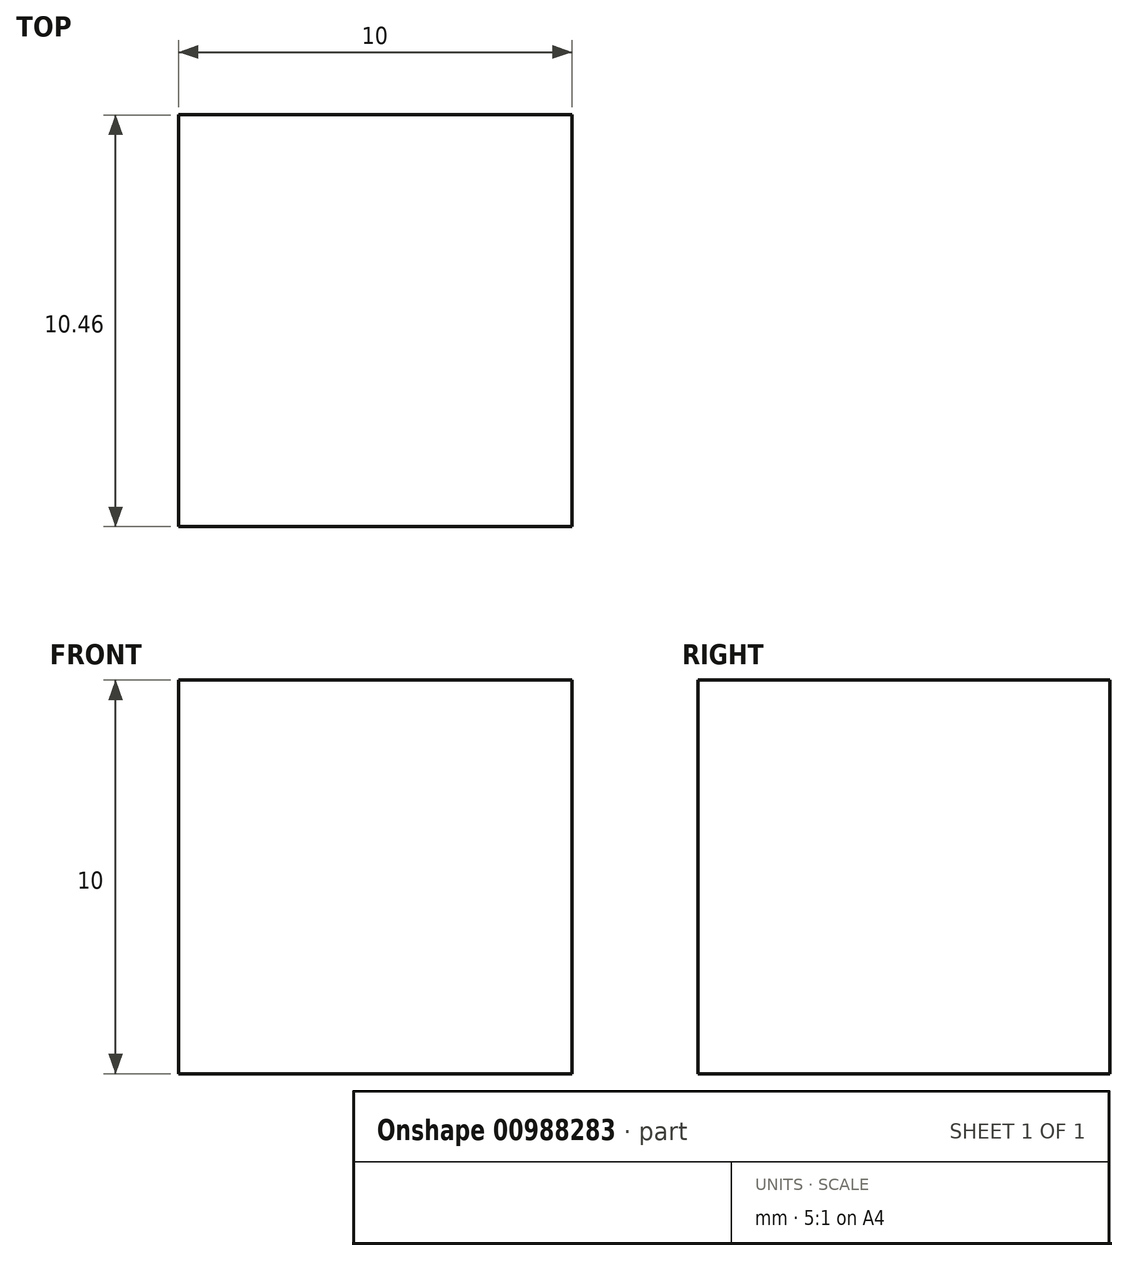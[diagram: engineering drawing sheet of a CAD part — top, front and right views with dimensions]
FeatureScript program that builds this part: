
annotation { "Feature Type Name" : "Feature", "Feature Type Description" : "" }
export const myFeature = defineFeature(function(context is Context, id is Id, definition is map)
    precondition{}
    {
        {
            var Q0;
            Q0=qCreatedBy(makeId("Top.planeOp"),FACE);
            var sketch = newSketch(context, id + "F0", { "sketchPlane" : qUnion([Q0])});
            skLineSegment(sketch, "E0.bottom", {"start": v(5, -5.23) * mm, "end": v(-5, -5.23) * mm});
            skLineSegment(sketch, "E0.top", {"start": v(5, 5.23) * mm, "end": v(-5, 5.23) * mm});
            skLineSegment(sketch, "E0.left", {"start": v(5, -5.23) * mm, "end": v(5, 5.23) * mm});
            skLineSegment(sketch, "E0.right", {"start": v(-5, -5.23) * mm, "end": v(-5, 5.23) * mm});
            skPoint(sketch, "E0.middle", {"position": v(0, 0) * mm});
            skSolve(sketch);
        }
        {
            var Q0;
            Q0=makeQuery(id+"F0.imprint","IMPRINT",FACE,{"disambiguationData":[TD([[makeQuery(id+"F0.imprint","IMPRINT",EDGE,{"derivedFrom":sQuery(id+"F0.wireOp",EDGE,"E0.bottom")}),-1.0]])]});
            extrude(context, id + "F1", {"entities" : qUnion([Q0]), "depth" : 10 * mm, "offsetDistance" : 25 * mm});
        }
    });
